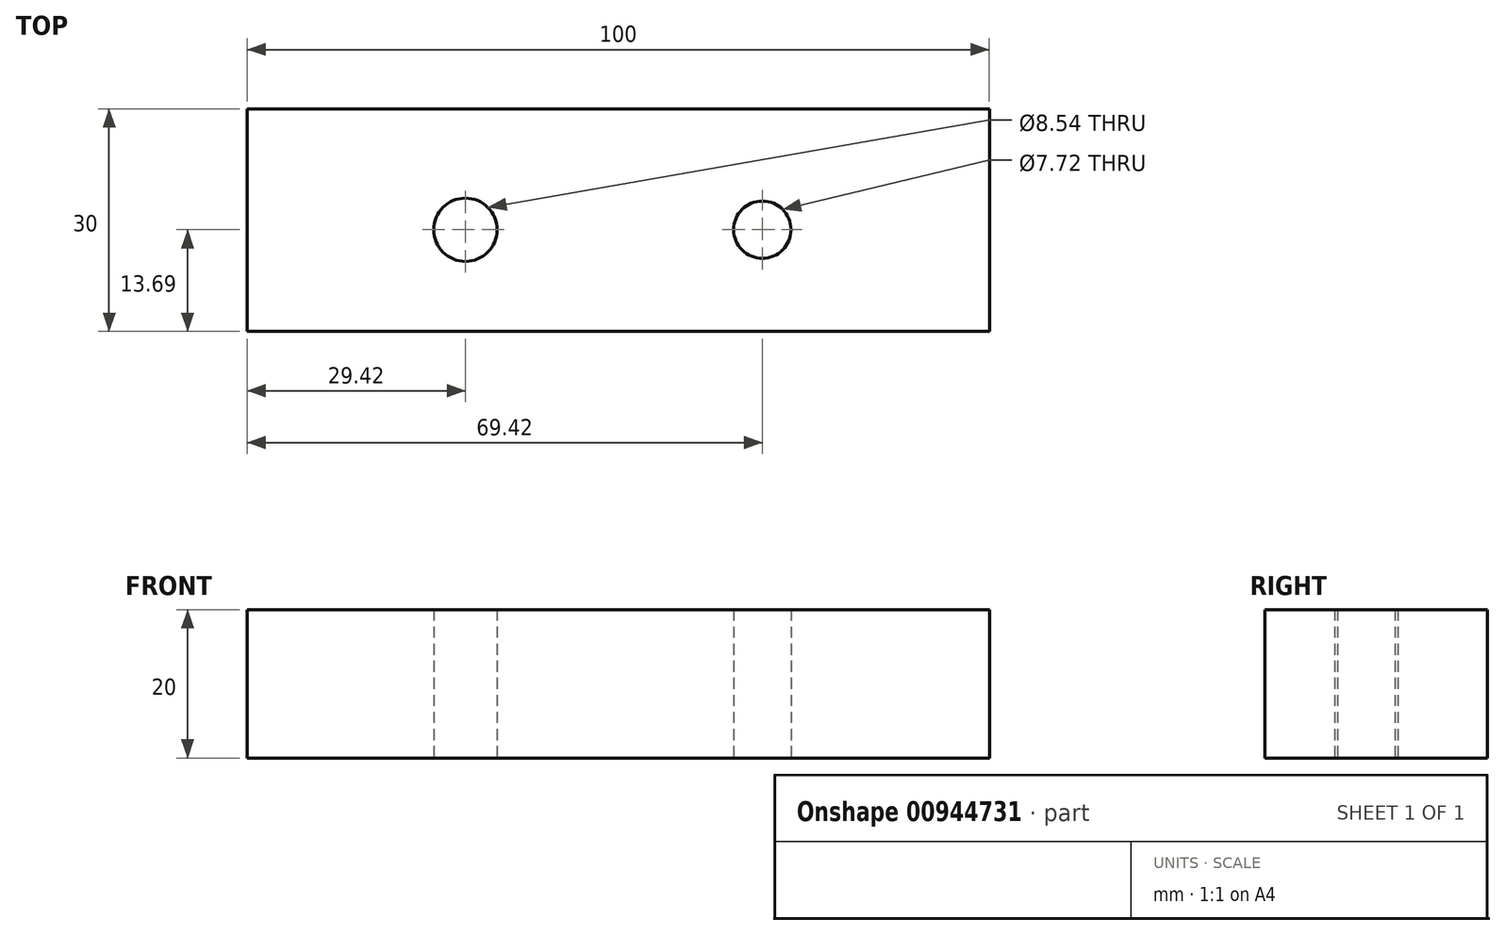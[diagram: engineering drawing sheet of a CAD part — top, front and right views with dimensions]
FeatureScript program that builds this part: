
annotation { "Feature Type Name" : "Feature", "Feature Type Description" : "" }
export const myFeature = defineFeature(function(context is Context, id is Id, definition is map)
    precondition{}
    {
        {
            var Q0;
            Q0=qCreatedBy(makeId("Top.planeOp"),FACE);
            var sketch = newSketch(context, id + "F0", { "sketchPlane" : qUnion([Q0])});
            skLineSegment(sketch, "E0.bottom", {"start": v(-49.42, 16.3) * mm, "end": v(50.58, 16.3) * mm});
            skLineSegment(sketch, "E0.top", {"start": v(-49.42, -13.7) * mm, "end": v(50.58, -13.7) * mm});
            skLineSegment(sketch, "E0.left", {"start": v(-49.42, 16.3) * mm, "end": v(-49.42, -13.7) * mm});
            skLineSegment(sketch, "E0.right", {"start": v(50.58, 16.3) * mm, "end": v(50.58, -13.7) * mm});
            skCircle(sketch, "E1", {"center": v(-20, 0) * mm, "radius": 4.27 * mm});
            skCircle(sketch, "E2", {"center": v(20, 0) * mm, "radius": 3.86 * mm});
            skLineSegment(sketch, "E3", {"start": v(0, 0) * mm, "end": v(20, 0) * mm, "construction": true});
            skLineSegment(sketch, "E4", {"start": v(0, 0) * mm, "end": v(-20, 0) * mm, "construction": true});
            skSolve(sketch);
        }
        {
            var Q0;
            Q0 = qSketchRegion(id + "F0", true);
            extrude(context, id + "F1", {"entities" : qUnion([Q0]), "depth" : 19.6 * mm, "offsetDistance" : 25 * mm});
        }
        {
            var Q0;
            Q0=makeQuery(id+"F1.opExtrude","CAP_FACE",FACE,{"disambiguationData":[OSD([sQuery(id+"F0.wireOp",EDGE,"E0.bottom"),sQuery(id+"F0.wireOp",EDGE,"E0.top"),sQuery(id+"F0.wireOp",EDGE,"E0.left"),sQuery(id+"F0.wireOp",EDGE,"E0.right"),sQuery(id+"F0.wireOp",EDGE,"E1"),sQuery(id+"F0.wireOp",EDGE,"E2")])],"isStart":false});
            extrude(context, id + "F2", {"entities" : qUnion([Q0]), "operationType" : NewBodyOperationType.ADD, "depth" : 0.4 * mm, "offsetDistance" : 25 * mm});
        }
    });
